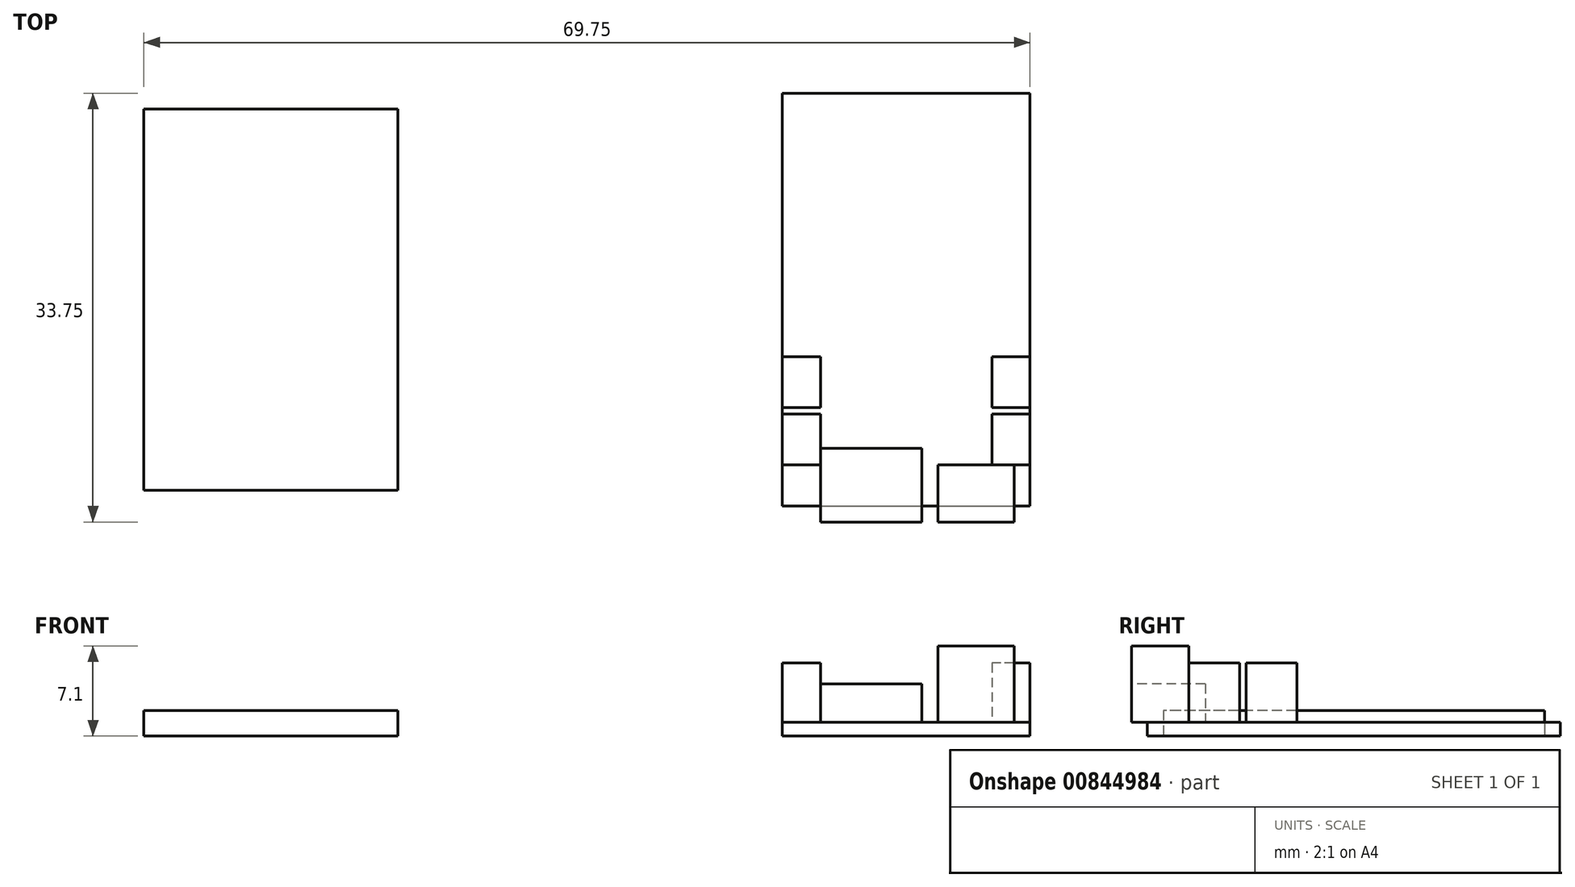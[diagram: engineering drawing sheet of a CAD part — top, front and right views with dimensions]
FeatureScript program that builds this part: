
annotation { "Feature Type Name" : "Feature", "Feature Type Description" : "" }
export const myFeature = defineFeature(function(context is Context, id is Id, definition is map)
    precondition{}
    {
        {
            var Q0;
            Q0=qCreatedBy(makeId("Top.planeOp"),FACE);
            var sketch = newSketch(context, id + "F0", { "sketchPlane" : qUnion([Q0])});
            skLineSegment(sketch, "E0.bottom", {"start": v(-9.75, 16.25) * mm, "end": v(9.75, 16.25) * mm});
            skLineSegment(sketch, "E0.top", {"start": v(-9.75, -16.25) * mm, "end": v(9.75, -16.25) * mm});
            skLineSegment(sketch, "E0.left", {"start": v(-9.75, 16.25) * mm, "end": v(-9.75, -16.25) * mm});
            skLineSegment(sketch, "E0.right", {"start": v(9.75, 16.25) * mm, "end": v(9.75, -16.25) * mm});
            skPoint(sketch, "E0.middle", {"position": v(0, 0) * mm});
            skLineSegment(sketch, "E1.bottom", {"start": v(-6.75, -11.7) * mm, "end": v(1.25, -11.7) * mm});
            skLineSegment(sketch, "E1.top", {"start": v(-6.75, -17.5) * mm, "end": v(1.25, -17.5) * mm});
            skLineSegment(sketch, "E1.left", {"start": v(-6.75, -11.7) * mm, "end": v(-6.75, -17.5) * mm});
            skLineSegment(sketch, "E1.right", {"start": v(1.25, -11.7) * mm, "end": v(1.25, -17.5) * mm});
            skLineSegment(sketch, "E2.bottom", {"start": v(-9.75, -4.5) * mm, "end": v(-6.75, -4.5) * mm});
            skLineSegment(sketch, "E2.top", {"start": v(-9.75, -8.5) * mm, "end": v(-6.75, -8.5) * mm});
            skLineSegment(sketch, "E2.left", {"start": v(-9.75, -4.5) * mm, "end": v(-9.75, -8.5) * mm});
            skLineSegment(sketch, "E2.right", {"start": v(-6.75, -4.5) * mm, "end": v(-6.75, -8.5) * mm});
            skLineSegment(sketch, "E3.bottom", {"start": v(-9.75, -9) * mm, "end": v(-6.75, -9) * mm});
            skLineSegment(sketch, "E3.top", {"start": v(-9.75, -13) * mm, "end": v(-6.75, -13) * mm});
            skLineSegment(sketch, "E3.left", {"start": v(-9.75, -9) * mm, "end": v(-9.75, -13) * mm});
            skLineSegment(sketch, "E3.right", {"start": v(-6.75, -9) * mm, "end": v(-6.75, -13) * mm});
            skLineSegment(sketch, "E4.MirrorCS", {"start": v(9.75, -4.5) * mm, "end": v(6.75, -4.5) * mm});
            skLineSegment(sketch, "E5.MirrorCS", {"start": v(6.75, -4.5) * mm, "end": v(6.75, -8.5) * mm});
            skLineSegment(sketch, "E6.MirrorCS", {"start": v(9.75, -8.5) * mm, "end": v(6.75, -8.5) * mm});
            skLineSegment(sketch, "E7.MirrorCS", {"start": v(6.75, -9) * mm, "end": v(6.75, -13) * mm});
            skLineSegment(sketch, "E8.MirrorCS", {"start": v(9.75, -9) * mm, "end": v(6.75, -9) * mm});
            skLineSegment(sketch, "E9.MirrorCS", {"start": v(9.75, -13) * mm, "end": v(6.75, -13) * mm});
            skLineSegment(sketch, "E10.bottom", {"start": v(2.5, -13) * mm, "end": v(8.5, -13) * mm});
            skLineSegment(sketch, "E10.top", {"start": v(2.5, -17.5) * mm, "end": v(8.5, -17.5) * mm});
            skLineSegment(sketch, "E10.left", {"start": v(2.5, -13) * mm, "end": v(2.5, -17.5) * mm});
            skLineSegment(sketch, "E10.right", {"start": v(8.5, -13) * mm, "end": v(8.5, -17.5) * mm});
            skSolve(sketch);
        }
        {
            var Q0;
            {var subQ3=sQuery(id+"F0.wireOp",EDGE,"E0.bottom");Q0=makeQuery(id+"F0.imprint","IMPRINT",FACE,{"disambiguationData":[TD([[makeQuery(id+"F0.imprint","IMPRINT",EDGE,{"derivedFrom":subQ3}),-1.0]])]});}
            var Q1;
            Q1=makeQuery(id+"F0.imprint","IMPRINT",FACE,{"disambiguationData":[TD([[makeQuery(id+"F0.imprint","IMPRINT",EDGE,{"derivedFrom":sQuery(id+"F0.wireOp",EDGE,"E2.bottom")}),-1.0]])]});
            var Q2;
            {var subQ2=sQuery(id+"F0.wireOp",EDGE,"E3.bottom");Q2=makeQuery(id+"F0.imprint","IMPRINT",FACE,{"disambiguationData":[TD([[makeQuery(id+"F0.imprint","IMPRINT",EDGE,{"derivedFrom":subQ2}),-1.0]])]});}
            var Q3;
            {var subQ5=sQuery(id+"F0.wireOp",EDGE,"E3.top");Q3=makeQuery(id+"F0.imprint","IMPRINT",FACE,{"disambiguationData":[TD([[makeQuery(id+"F0.imprint","IMPRINT",EDGE,{"derivedFrom":subQ5}),-1.0]])]});}
            var Q4;
            {var subQ1=sQuery(id+"F0.wireOp",EDGE,"E1.bottom");Q4=makeQuery(id+"F0.imprint","IMPRINT",FACE,{"disambiguationData":[TD([[makeQuery(id+"F0.imprint","IMPRINT",EDGE,{"derivedFrom":subQ1}),-1.0]])]});}
            var Q5;
            {var subQ0=sQuery(id+"F0.wireOp",EDGE,"E10.left");var subQ3=sQuery(id+"F0.wireOp",EDGE,"E0.top");var subQ4=makeQuery(id+"F0.imprint","INTERSECT",VERTEX,{"derivedFrom":[subQ3,subQ0]});Q5=makeQuery(id+"F0.imprint","IMPRINT",FACE,{"disambiguationData":[TD([[makeQuery(id+"F0.imprint","IMPRINT",EDGE,{"disambiguationData":[TD([[subQ4,-1.0]])],"derivedFrom":subQ3}),1.0]])]});}
            var Q6;
            {var subQ5=sQuery(id+"F0.wireOp",EDGE,"E9.MirrorCS");Q6=makeQuery(id+"F0.imprint","IMPRINT",FACE,{"disambiguationData":[TD([[makeQuery(id+"F0.imprint","IMPRINT",EDGE,{"derivedFrom":subQ5}),1.0]])]});}
            var Q7;
            {var subQ3=sQuery(id+"F0.wireOp",EDGE,"E7.MirrorCS");Q7=makeQuery(id+"F0.imprint","IMPRINT",FACE,{"disambiguationData":[TD([[makeQuery(id+"F0.imprint","IMPRINT",EDGE,{"derivedFrom":subQ3}),1.0]])]});}
            var Q8;
            {var subQ0=sQuery(id+"F0.wireOp",EDGE,"E4.MirrorCS");Q8=makeQuery(id+"F0.imprint","IMPRINT",FACE,{"disambiguationData":[TD([[makeQuery(id+"F0.imprint","IMPRINT",EDGE,{"derivedFrom":subQ0}),1.0]])]});}
            extrude(context, id + "F1", {"entities" : qUnion([Q0, Q1, Q2, Q3, Q4, Q5, Q6, Q7, Q8]), "depth" : 1.1 * mm, "offsetDistance" : 25 * mm});
        }
        {
            var Q0;
            {var subQ1=sQuery(id+"F0.wireOp",EDGE,"E1.bottom");Q0=makeQuery(id+"F0.imprint","IMPRINT",FACE,{"disambiguationData":[TD([[makeQuery(id+"F0.imprint","IMPRINT",EDGE,{"derivedFrom":subQ1}),-1.0]])]});}
            var Q1;
            {var subQ5=sQuery(id+"F0.wireOp",EDGE,"E1.top");Q1=makeQuery(id+"F0.imprint","IMPRINT",FACE,{"disambiguationData":[TD([[makeQuery(id+"F0.imprint","IMPRINT",EDGE,{"derivedFrom":subQ5}),1.0]])]});}
            var Q2;
            Q2=makeQuery(id+"F1.opExtrude","CAP_FACE",FACE,{"disambiguationData":[OSD([sQuery(id+"F0.wireOp",EDGE,"E0.bottom"),sQuery(id+"F0.wireOp",EDGE,"E0.top"),sQuery(id+"F0.wireOp",EDGE,"E0.left"),sQuery(id+"F0.wireOp",EDGE,"E0.right"),sQuery(id+"F0.wireOp",EDGE,"E2.left"),sQuery(id+"F0.wireOp",EDGE,"E3.left")])],"isStart":false});
            var Q3;
            Q3=makeQuery(id+"F1.opExtrude","CAP_FACE",FACE,{"disambiguationData":[OSD([sQuery(id+"F0.wireOp",EDGE,"E0.bottom"),sQuery(id+"F0.wireOp",EDGE,"E0.top"),sQuery(id+"F0.wireOp",EDGE,"E0.left"),sQuery(id+"F0.wireOp",EDGE,"E0.right"),sQuery(id+"F0.wireOp",EDGE,"E2.left"),sQuery(id+"F0.wireOp",EDGE,"E3.left")])],"isStart":false});
            extrude(context, id + "F2", {"entities" : qUnion([Q0, Q1]), "endBound" : BoundingType.UP_TO_SURFACE, "depth" : 25 * mm, "endBoundEntityFace" : qUnion([Q2]), "hasOffset" : true, "offsetDistance" : 3 * mm, "offsetOppositeDirection" : true, "hasSecondDirection" : true, "secondDirectionBound" : SecondDirectionBoundingType.UP_TO_SURFACE, "secondDirectionOppositeDirection" : false, "secondDirectionDepth" : 25 * mm, "secondDirectionBoundEntityFace" : qUnion([Q3])});
        }
        {
            var Q0;
            {var subQ2=sQuery(id+"F0.wireOp",EDGE,"E3.bottom");Q0=makeQuery(id+"F0.imprint","IMPRINT",FACE,{"disambiguationData":[TD([[makeQuery(id+"F0.imprint","IMPRINT",EDGE,{"derivedFrom":subQ2}),-1.0]])]});}
            var Q1;
            Q1=makeQuery(id+"F0.imprint","IMPRINT",FACE,{"disambiguationData":[TD([[makeQuery(id+"F0.imprint","IMPRINT",EDGE,{"derivedFrom":sQuery(id+"F0.wireOp",EDGE,"E2.bottom")}),-1.0]])]});
            var Q2;
            {var subQ3=sQuery(id+"F0.wireOp",EDGE,"E7.MirrorCS");Q2=makeQuery(id+"F0.imprint","IMPRINT",FACE,{"disambiguationData":[TD([[makeQuery(id+"F0.imprint","IMPRINT",EDGE,{"derivedFrom":subQ3}),1.0]])]});}
            var Q3;
            {var subQ0=sQuery(id+"F0.wireOp",EDGE,"E4.MirrorCS");Q3=makeQuery(id+"F0.imprint","IMPRINT",FACE,{"disambiguationData":[TD([[makeQuery(id+"F0.imprint","IMPRINT",EDGE,{"derivedFrom":subQ0}),1.0]])]});}
            var Q4;
            Q4=makeQuery(id+"F1.opExtrude","CAP_FACE",FACE,{"disambiguationData":[OSD([sQuery(id+"F0.wireOp",EDGE,"E0.bottom"),sQuery(id+"F0.wireOp",EDGE,"E0.top"),sQuery(id+"F0.wireOp",EDGE,"E0.left"),sQuery(id+"F0.wireOp",EDGE,"E0.right"),sQuery(id+"F0.wireOp",EDGE,"E2.left"),sQuery(id+"F0.wireOp",EDGE,"E3.left")])],"isStart":false});
            var Q5;
            Q5=makeQuery(id+"F1.opExtrude","CAP_FACE",FACE,{"disambiguationData":[OSD([sQuery(id+"F0.wireOp",EDGE,"E0.bottom"),sQuery(id+"F0.wireOp",EDGE,"E0.top"),sQuery(id+"F0.wireOp",EDGE,"E0.left"),sQuery(id+"F0.wireOp",EDGE,"E0.right"),sQuery(id+"F0.wireOp",EDGE,"E2.left"),sQuery(id+"F0.wireOp",EDGE,"E3.left")])],"isStart":false});
            extrude(context, id + "F3", {"entities" : qUnion([Q0, Q1, Q2, Q3]), "endBound" : BoundingType.UP_TO_SURFACE, "depth" : 25 * mm, "endBoundEntityFace" : qUnion([Q4]), "hasOffset" : true, "offsetDistance" : 4.65 * mm, "offsetOppositeDirection" : true, "hasSecondDirection" : true, "secondDirectionBound" : SecondDirectionBoundingType.UP_TO_SURFACE, "secondDirectionOppositeDirection" : false, "secondDirectionDepth" : 25 * mm, "secondDirectionBoundEntityFace" : qUnion([Q5])});
        }
        {
            var Q0;
            {var subQ0=sQuery(id+"F0.wireOp",EDGE,"E10.left");var subQ3=sQuery(id+"F0.wireOp",EDGE,"E0.top");var subQ4=makeQuery(id+"F0.imprint","INTERSECT",VERTEX,{"derivedFrom":[subQ3,subQ0]});Q0=makeQuery(id+"F0.imprint","IMPRINT",FACE,{"disambiguationData":[TD([[makeQuery(id+"F0.imprint","IMPRINT",EDGE,{"disambiguationData":[TD([[subQ4,-1.0]])],"derivedFrom":subQ3}),1.0]])]});}
            var Q1;
            {var subQ5=sQuery(id+"F0.wireOp",EDGE,"E10.top");Q1=makeQuery(id+"F0.imprint","IMPRINT",FACE,{"disambiguationData":[TD([[makeQuery(id+"F0.imprint","IMPRINT",EDGE,{"derivedFrom":subQ5}),1.0]])]});}
            var Q2;
            Q2=makeQuery(id+"F1.opExtrude","CAP_FACE",FACE,{"disambiguationData":[OSD([sQuery(id+"F0.wireOp",EDGE,"E0.bottom"),sQuery(id+"F0.wireOp",EDGE,"E0.top"),sQuery(id+"F0.wireOp",EDGE,"E0.left"),sQuery(id+"F0.wireOp",EDGE,"E0.right"),sQuery(id+"F0.wireOp",EDGE,"E2.left"),sQuery(id+"F0.wireOp",EDGE,"E3.left")])],"isStart":false});
            var Q3;
            Q3=makeQuery(id+"F1.opExtrude","CAP_FACE",FACE,{"disambiguationData":[OSD([sQuery(id+"F0.wireOp",EDGE,"E0.bottom"),sQuery(id+"F0.wireOp",EDGE,"E0.top"),sQuery(id+"F0.wireOp",EDGE,"E0.left"),sQuery(id+"F0.wireOp",EDGE,"E0.right"),sQuery(id+"F0.wireOp",EDGE,"E2.left"),sQuery(id+"F0.wireOp",EDGE,"E3.left")])],"isStart":false});
            extrude(context, id + "F4", {"entities" : qUnion([Q0, Q1]), "endBound" : BoundingType.UP_TO_SURFACE, "depth" : 25 * mm, "endBoundEntityFace" : qUnion([Q2]), "hasOffset" : true, "offsetDistance" : 6 * mm, "offsetOppositeDirection" : true, "hasSecondDirection" : true, "secondDirectionBound" : SecondDirectionBoundingType.UP_TO_SURFACE, "secondDirectionOppositeDirection" : false, "secondDirectionDepth" : 25 * mm, "secondDirectionBoundEntityFace" : qUnion([Q3])});
        }
        {
            var Q0;
            Q0=qCreatedBy(makeId("Top.planeOp"),FACE);
            var sketch = newSketch(context, id + "F5", { "sketchPlane" : qUnion([Q0])});
            skLineSegment(sketch, "E11.bottom", {"start": v(-60, 15) * mm, "end": v(-40, 15) * mm});
            skLineSegment(sketch, "E11.top", {"start": v(-60, -15) * mm, "end": v(-40, -15) * mm});
            skLineSegment(sketch, "E11.left", {"start": v(-60, 15) * mm, "end": v(-60, -15) * mm});
            skLineSegment(sketch, "E11.right", {"start": v(-40, 15) * mm, "end": v(-40, -15) * mm});
            skPoint(sketch, "E11.middle", {"position": v(-50, 0) * mm});
            skSolve(sketch);
        }
        {
            var Q0;
            Q0=makeQuery(id+"F5.imprint","IMPRINT",FACE,{"disambiguationData":[TD([[makeQuery(id+"F5.imprint","IMPRINT",EDGE,{"derivedFrom":sQuery(id+"F5.wireOp",EDGE,"E11.bottom")}),-1.0]])]});
            extrude(context, id + "F6", {"entities" : qUnion([Q0]), "depth" : 2 * mm, "offsetDistance" : 25 * mm});
        }
    });
